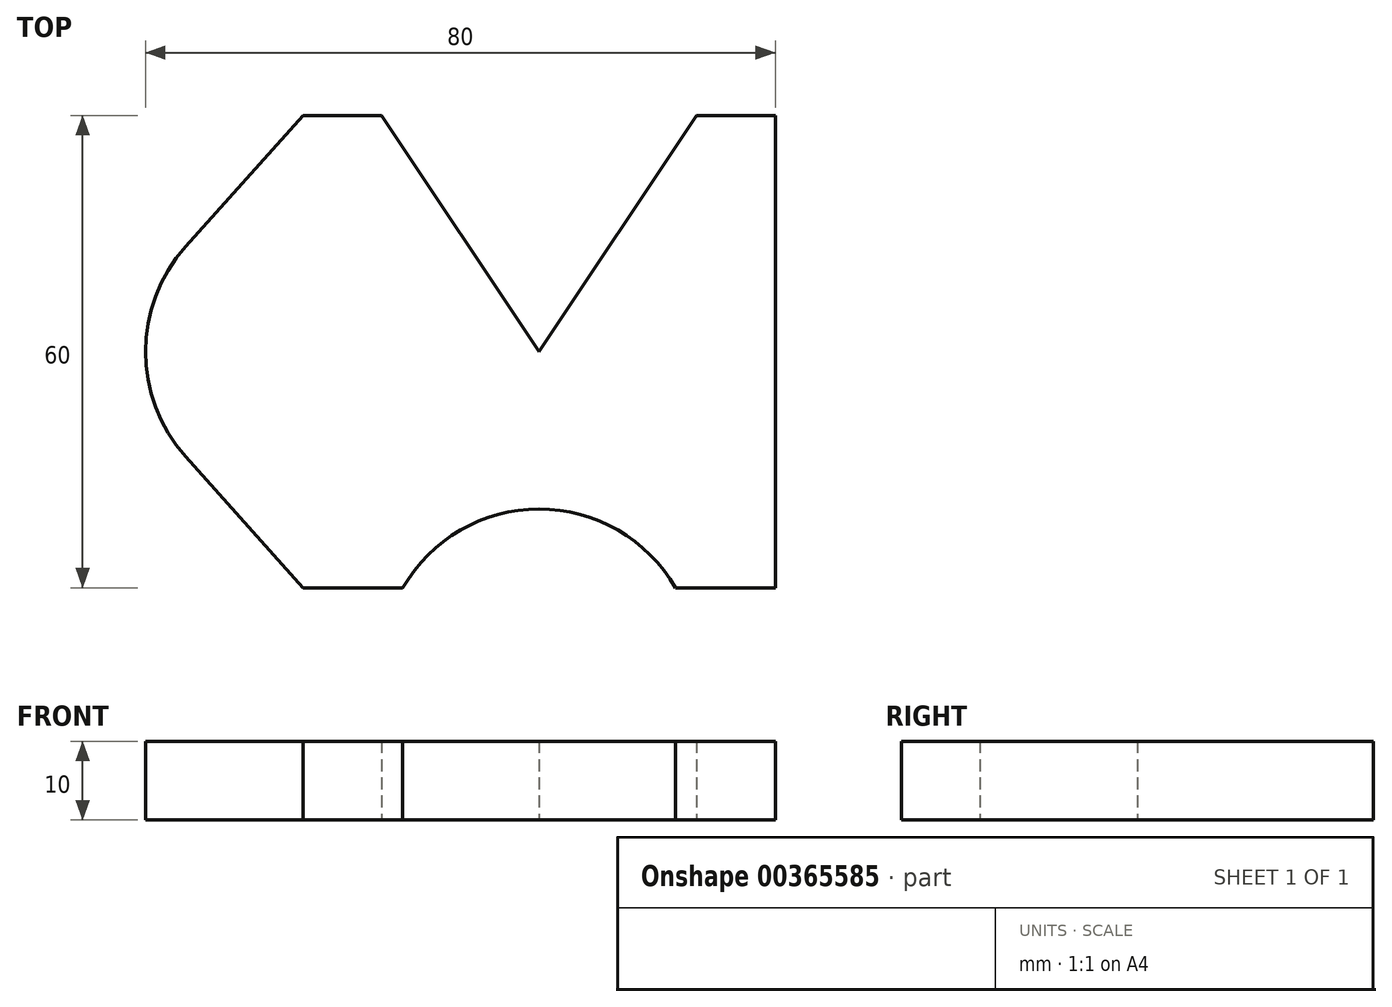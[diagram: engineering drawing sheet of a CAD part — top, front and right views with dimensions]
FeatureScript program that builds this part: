
annotation { "Feature Type Name" : "Feature", "Feature Type Description" : "" }
export const myFeature = defineFeature(function(context is Context, id is Id, definition is map)
    precondition{}
    {
        {
            var Q0;
            Q0=qCreatedBy(makeId("Top.planeOp"),FACE);
            var sketch = newSketch(context, id + "F0", { "sketchPlane" : qUnion([Q0])});
            skLineSegment(sketch, "E0", {"start": v(0, 0) * mm, "end": v(20, 30) * mm});
            skLineSegment(sketch, "E1", {"start": v(20, 30) * mm, "end": v(30, 30) * mm});
            skLineSegment(sketch, "E2", {"start": v(30, 30) * mm, "end": v(30, -30) * mm});
            skLineSegment(sketch, "E3", {"start": v(30, -30) * mm, "end": v(17.32, -30) * mm});
            skArc(sketch, "E4", {"start": v(17.32, -30) * mm, "mid": v(0, -20) * mm, "end": v(-17.32, -30) * mm});
            skLineSegment(sketch, "E5", {"start": v(-17.32, -30) * mm, "end": v(-30, -30) * mm});
            skLineSegment(sketch, "E6", {"start": v(-30, 30) * mm, "end": v(-20, 30) * mm});
            skLineSegment(sketch, "E7", {"start": v(-20, 30) * mm, "end": v(0, 0) * mm});
            skLineSegment(sketch, "E8", {"start": v(-30, -30) * mm, "end": v(-44.9, -13.33) * mm});
            skLineSegment(sketch, "E9", {"start": v(-30, 30) * mm, "end": v(-44.9, 13.33) * mm});
            skArc(sketch, "E10", {"start": v(-44.9, 13.33) * mm, "mid": v(-50, 0) * mm, "end": v(-44.9, -13.33) * mm});
            skSolve(sketch);
        }
        {
            var Q0;
            Q0 = qSketchRegion(id + "F0", true);
            extrude(context, id + "F1", {"entities" : qUnion([Q0]), "depth" : 10 * mm, "offsetDistance" : 25 * mm});
        }
    });
